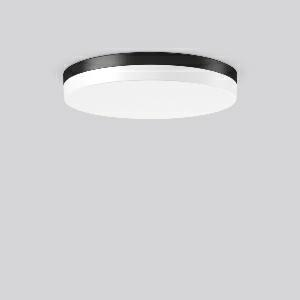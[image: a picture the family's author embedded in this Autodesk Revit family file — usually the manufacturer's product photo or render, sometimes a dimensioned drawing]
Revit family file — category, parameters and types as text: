
# Revit family: flat_slim_round_312634_0031_730_4fc9
name_source: partatom
category: Lighting Fixtures
units: mm (PartAtom-declared; Revit-internal decimal feet)

## family parameters
Cut with Voids When Loaded = No
Host = Face
Light Source = No
Part Type = Normal
Room Calculation Point = No
Round Connector Dimension = Use Diameter
Shared = No

## types (1)
- MultiLumen 1 830 (1 x LED Modul 830, 3450 lm, 3000)
    Apparent Load = 26 VA
    CIE Flux Codes = 40 71 90 84 100
    Color Rendering = 80
    Color Temperature = 3000
    Default Elevation = 1800 mm
    Height = 70 mm
    Lamp = 1 x LED Modul 830
    Lamp Light Flux = 3450 lm
    Lamp count = 1
    Length = 480 mm
    Lifetime = 50000 h
    Luminous efficacy = 133 lm/W
    Manufacturer = RZB
    ModVariant = No
    Model = 312634.0031.730
    Mounting Place = Ceiling
    Mounting Type = Surface mounted
    Number of Poles = 1
    OnlyDefault = Yes
    Power Factor = 1
    Product Name = FLAT SLIM round
    Product group = Surface mounted ceiling and wall luminaires
    ProductGroupID = 305
    Protection Class = Protection class I
    Protection Degree = Degree of protection
    RLX_Detail_Level = 1
    RLX_Emergency_Light_Flux = 0 lm
    RLX_Emergency_Type = 0
    RLX_Emergency_Type_DB = No
    RlxData = <blob elided: 23281 chars, md5=3ca82539>
    Socket = socket
    Standby Power = 0 W
    System Light Flux = 3450 lm
    System Power = 26 W
    Type Comments = MultiLumen 1 830
    Type Image = 312633.0031.jpg
    URL = http://relux.com
    VarID = multilumen_1_830
    Voltage = 0 V
    Weight = 0.00 kg
    Width = 0 mm  [stored 0 ft]

note: [stored X ft] marks values corroborated as IEEE doubles in the binary element streams (Revit-internal decimal feet)

## geometry (parser evidence)
native form markers: Blend x4, Sweep x12
no freeform markers — native parametric forms only
